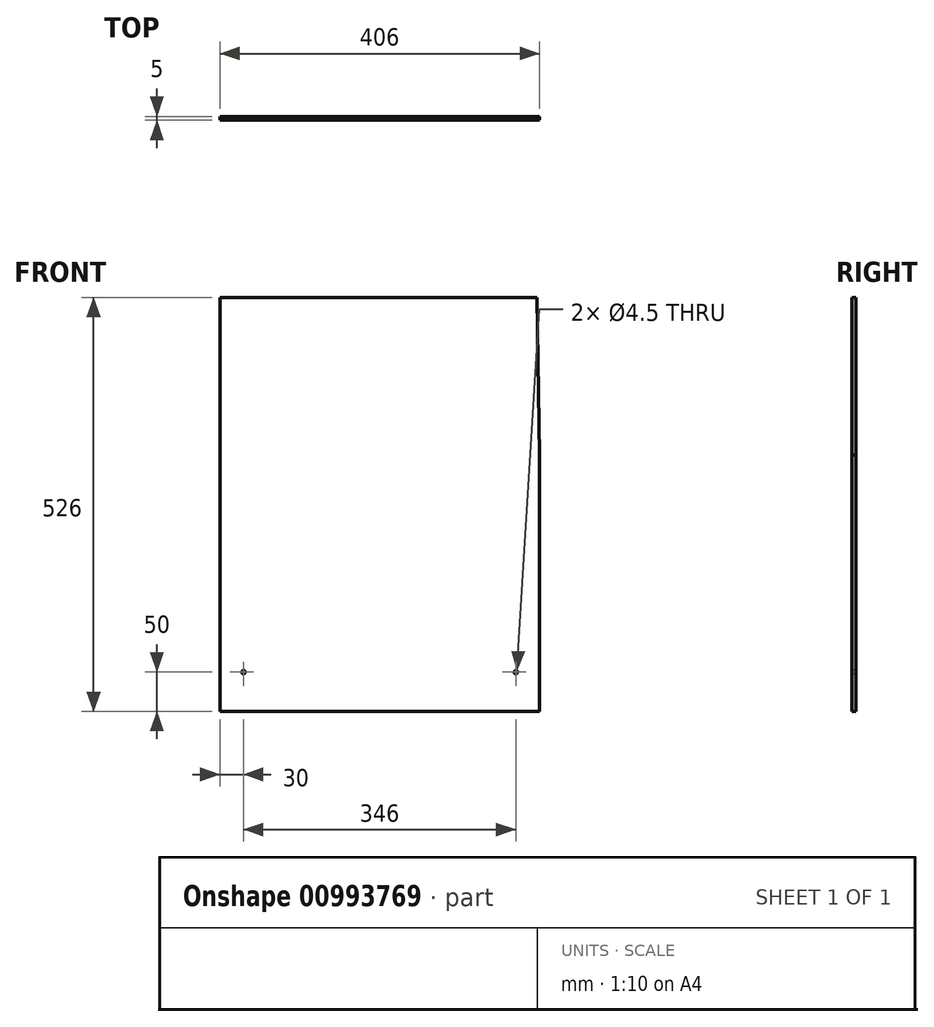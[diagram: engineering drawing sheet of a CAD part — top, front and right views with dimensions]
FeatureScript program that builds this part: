
annotation { "Feature Type Name" : "Feature", "Feature Type Description" : "" }
export const myFeature = defineFeature(function(context is Context, id is Id, definition is map)
    precondition{}
    {
        {
            var Q0;
            Q0=qCreatedBy(makeId("Front.planeOp"),FACE);
            var sketch = newSketch(context, id + "F0", { "sketchPlane" : qUnion([Q0])});
            skLineSegment(sketch, "E0.bottom", {"start": v(0, 0) * mm, "end": v(406, 0) * mm});
            skLineSegment(sketch, "E0.top", {"start": v(0, 526) * mm, "end": v(403, 526) * mm});
            skLineSegment(sketch, "E0.left", {"start": v(0, 0) * mm, "end": v(0, 526) * mm});
            skLineSegment(sketch, "E0.right", {"start": v(406, 0) * mm, "end": v(406, 326) * mm});
            skLineSegment(sketch, "E1", {"start": v(403, 526) * mm, "end": v(406, 326) * mm});
            skSolve(sketch);
        }
        {
            var Q0;
            Q0=makeQuery(id+"F0.imprint","IMPRINT",FACE,{"disambiguationData":[TD([[makeQuery(id+"F0.imprint","IMPRINT",EDGE,{"derivedFrom":sQuery(id+"F0.wireOp",EDGE,"E0.bottom")}),1.0]])]});
            var Q1;
            Q1=makeQuery(id+"F0.imprint","IMPRINT",FACE,{"disambiguationData":[TD([[makeQuery(id+"F0.imprint","IMPRINT",EDGE,{"derivedFrom":sQuery(id+"F0.wireOp",EDGE,"tbrh48hv-wd16-6U3q-6ftw-UJMhu88pGy1S.bottom")}),-1.0]])]});
            var Q2;
            Q2=makeQuery(id+"F0.imprint","IMPRINT",FACE,{"disambiguationData":[TD([[makeQuery(id+"F0.imprint","IMPRINT",EDGE,{"derivedFrom":sQuery(id+"F0.wireOp",EDGE,"3kSVMK98-RxYE-l63r-zHFi-MemegGt4laL0.bottom")}),-1.0]])]});
            extrude(context, id + "F1", {"entities" : qUnion([Q0, Q1, Q2]), "depth" : 5 * mm, "offsetDistance" : 25 * mm});
        }
        {
            var Q0;
            Q0=makeQuery(id+"F1.opExtrude","CAP_FACE",FACE,{"disambiguationData":[OSD([sQuery(id+"F0.wireOp",EDGE,"E0.bottom"),sQuery(id+"F0.wireOp",EDGE,"E0.top"),sQuery(id+"F0.wireOp",EDGE,"E0.left"),sQuery(id+"F0.wireOp",EDGE,"E0.right"),sQuery(id+"F0.wireOp",EDGE,"E1")])],"isStart":false});
            var sketch = newSketch(context, id + "F2", { "sketchPlane" : qUnion([Q0])});
            skCircle(sketch, "E2", {"center": v(30, 50) * mm, "radius": 2.25 * mm});
            skCircle(sketch, "E3", {"center": v(376, 50) * mm, "radius": 2.25 * mm});
            skSolve(sketch);
        }
        {
            var Q0;
            Q0=makeQuery(id+"F2.imprint","IMPRINT",FACE,{"disambiguationData":[TD([[makeQuery(id+"F2.imprint","IMPRINT",EDGE,{"derivedFrom":sQuery(id+"F2.wireOp",EDGE,"E2")}),1.0]])]});
            var Q1;
            Q1=makeQuery(id+"F2.imprint","IMPRINT",FACE,{"disambiguationData":[TD([[makeQuery(id+"F2.imprint","IMPRINT",EDGE,{"derivedFrom":sQuery(id+"F2.wireOp",EDGE,"E3")}),1.0]])]});
            var Q2;
            Q2=makeQuery(id+"F1.opExtrude","CAP_FACE",FACE,{"disambiguationData":[OSD([sQuery(id+"F0.wireOp",EDGE,"E0.bottom"),sQuery(id+"F0.wireOp",EDGE,"E0.top"),sQuery(id+"F0.wireOp",EDGE,"E0.left"),sQuery(id+"F0.wireOp",EDGE,"E0.right"),sQuery(id+"F0.wireOp",EDGE,"E1")])],"isStart":true});
            extrude(context, id + "F3", {"entities" : qUnion([Q0, Q1]), "operationType" : NewBodyOperationType.REMOVE, "endBound" : BoundingType.UP_TO_SURFACE, "oppositeDirection" : true, "depth" : 25 * mm, "endBoundEntityFace" : qUnion([Q2]), "offsetDistance" : 25 * mm});
        }
    });
